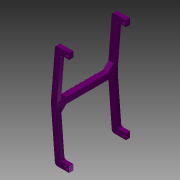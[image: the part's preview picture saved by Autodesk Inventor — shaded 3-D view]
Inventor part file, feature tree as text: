
AUTODESK INVENTOR PART (.ipt)
format: ipt  version: 2015 (Build 190159000, 159)  size: 342,528 bytes
history: native  units: mm
features: extrude x4, sketch x4, plane x2, mirror x2, fillet x1
ambient origin geometry x8: Origin, YZ Plane, XZ Plane, XY Plane, X Axis, Y Axis, Z Axis, Center Point
bodies: Body1 (feature_tree)
feature tree (13):
  extrude  "Extrusion11"  Depth=5.0mm
  extrude  "Extrusion12"  Depth=13.585143mm
  plane  "Work Plane10"
  extrude  "Extrusion13"  Depth=7.5mm
  plane  "Work Plane11"
  mirror  "Mirror5"
  fillet  "Fillet15"  Radius=2.5mm
  mirror  "Mirror6"
  extrude  "Extrusion14"  Depth=3.5mm TaperAngle=0.0deg
  sketch  "Sketch1"  dims[d4=3.5mm d8=5.0mm]
  sketch  "Sketch5"  dims[d9=5.0mm d16=13.585143mm]
  sketch  "Sketch6"  dims[d20=2.5mm d62=7.5mm d63=2.5mm]
  sketch  "Sketch7"  dims[d64=2.0mm d65=3.5mm d66=0.0mm d67=5.0mm d68=5.0mm d69=22.75mm d70=0.0mm d71=-33.25mm d72=5.0mm d73=90.0deg d74=45.0deg d75=4.35mm d76=0.0mm d77=0.0mm d78=0.5mm d79=1.0mm d80=0.0mm d81=22.75mm]
